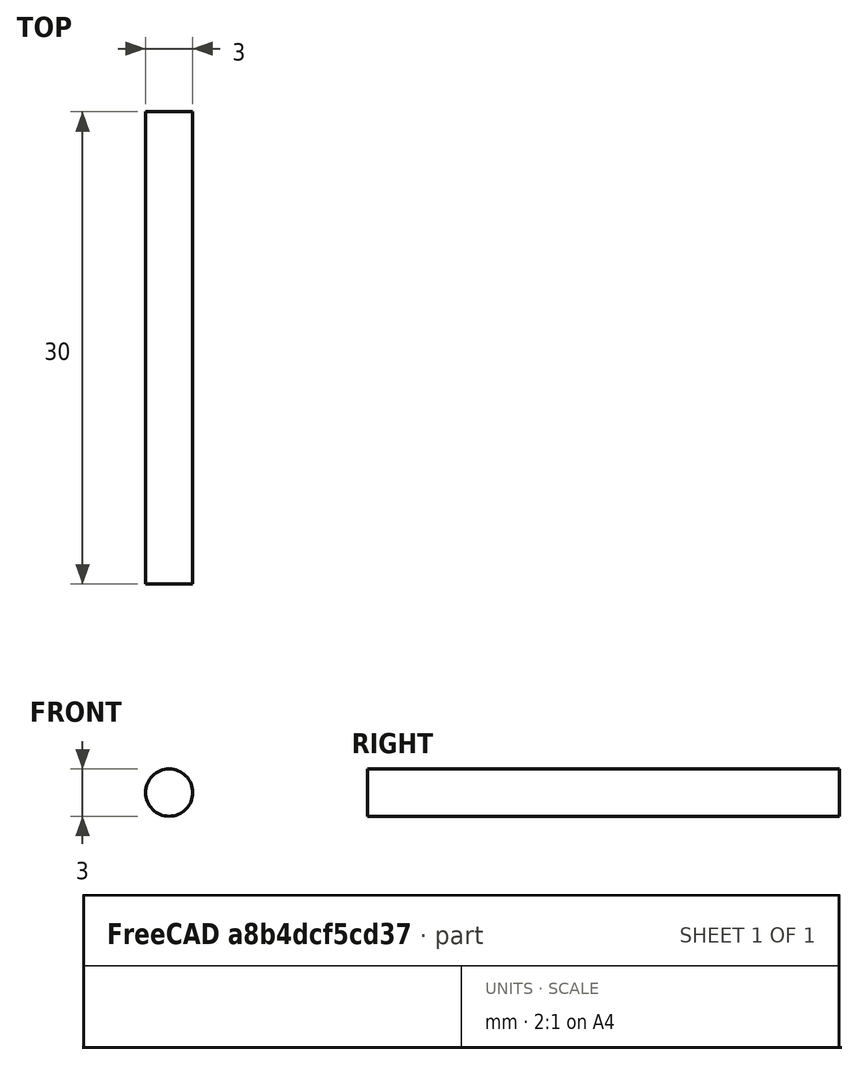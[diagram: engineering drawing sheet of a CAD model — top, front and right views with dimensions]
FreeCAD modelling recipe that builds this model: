
FCSTD DOCUMENT  (FreeCAD 1.0R39109 (Git))
Label: stift
License: All rights reserved
objects: Sketcher::SketchObject×1, PartDesign::Pad×1, PartDesign::Body×1
note: 6 computed .brp shape members not serialized (recipe doc carries the construction recipe); baked Part::Feature solids carry a one-line shape summary decoded from their .brp

FEATURE [Sketcher::SketchObject] Sketch
  ArcFitTolerance = 1e-06
  AttachmentSupport = -> [XZ_Plane]
  FullyConstrained = true
  MakeInternals = false
  MapMode = 5
  Placement = pos=(0,0,0) rot=(1,0,0;1.5708rad)
  sketch-geometry (1):
    g0: Circle CenterX=0 CenterY=0 CenterZ=0 NormalX=0 NormalY=0 NormalZ=1 AngleXU=0 Radius=1.5
  constraints (2):
    c: Coincident(g0,g-1)
    c: Diameter(g0) = 3
FEATURE [PartDesign::Pad] Pad
  Direction = (0,-1,2e-16)
  Length = 30
  Length2 = 10
  Placement = pos=(0,0,0) rot=(1,0,0;1.5708rad)
  Profile = -> Sketch
  ReferenceAxis = -> Sketch [N_Axis]
  Reversed = true
  Suppressed = false
  Type = 0
FEATURE [PartDesign::Body] Body  label="Körper"
  AllowCompound = false
  Group = -> [Sketch,Pad]
  Origin = -> Origin
  Tip = -> Pad
